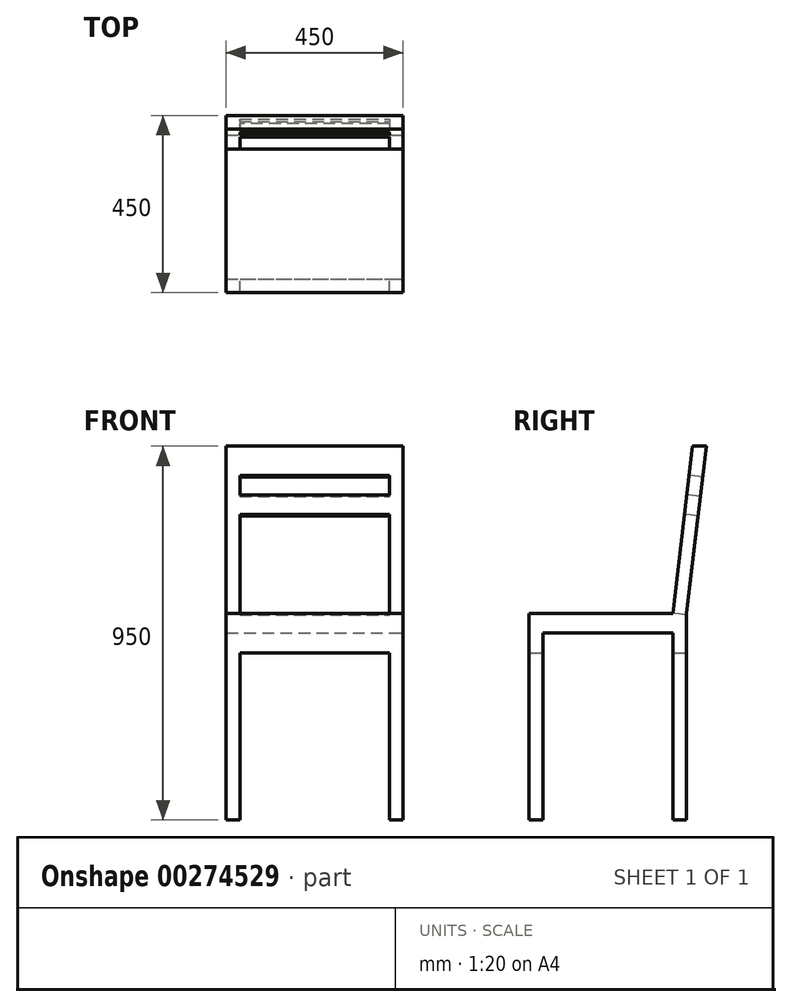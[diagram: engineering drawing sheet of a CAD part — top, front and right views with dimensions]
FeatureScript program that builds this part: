
annotation { "Feature Type Name" : "Feature", "Feature Type Description" : "" }
export const myFeature = defineFeature(function(context is Context, id is Id, definition is map)
    precondition{}
    {
        {
            var Q0;
            Q0=qCreatedBy(makeId("Top.planeOp"),FACE);
            var sketch = newSketch(context, id + "F0", { "sketchPlane" : qUnion([Q0])});
            skLineSegment(sketch, "E0.bottom", {"start": v(225, 225) * mm, "end": v(-225, 225) * mm});
            skLineSegment(sketch, "E0.top", {"start": v(225, -225) * mm, "end": v(-225, -225) * mm});
            skLineSegment(sketch, "E0.left", {"start": v(225, 225) * mm, "end": v(225, -225) * mm});
            skLineSegment(sketch, "E0.right", {"start": v(-225, 225) * mm, "end": v(-225, -225) * mm});
            skPoint(sketch, "E0.middle", {"position": v(0, 0) * mm});
            skSolve(sketch);
        }
        {
            var Q0;
            Q0=qSketchRegion(id+"F0",true);
            extrude(context, id + "F1", {"entities" : qUnion([Q0]), "depth" : 950 * mm});
        }
        {
            var Q0;
            Q0=makeQuery(id+"F1.opExtrude","SWEPT_FACE",FACE,{"disambiguationData":[OSD([sQuery(id+"F0.wireOp",EDGE,"E0.left")])]});
            var sketch = newSketch(context, id + "F2", { "sketchPlane" : qUnion([Q0])});
            skLineSegment(sketch, "E1.bottom", {"start": v(225, 475) * mm, "end": v(-225, 475) * mm});
            skLineSegment(sketch, "E1.top", {"start": v(225, 525) * mm, "end": v(-225, 525) * mm});
            skLineSegment(sketch, "E1.left", {"start": v(225, 475) * mm, "end": v(225, 525) * mm});
            skLineSegment(sketch, "E1.right", {"start": v(-225, 475) * mm, "end": v(-225, 525) * mm});
            skLineSegment(sketch, "E2", {"start": v(225, 950) * mm, "end": v(175, 525) * mm});
            skLineSegment(sketch, "E3", {"start": v(190, 950) * mm, "end": v(140, 525) * mm});
            skLineSegment(sketch, "E4", {"start": v(175, 525) * mm, "end": v(175, 0) * mm});
            skLineSegment(sketch, "E5", {"start": v(140, 525) * mm, "end": v(140, 0) * mm});
            skLineSegment(sketch, "E6.bottom", {"start": v(-225, 475) * mm, "end": v(-190, 475) * mm});
            skLineSegment(sketch, "E6.top", {"start": v(-225, 0) * mm, "end": v(-190, 0) * mm});
            skLineSegment(sketch, "E6.left", {"start": v(-225, 475) * mm, "end": v(-225, 0) * mm});
            skLineSegment(sketch, "E6.right", {"start": v(-190, 475) * mm, "end": v(-190, 0) * mm});
            skSolve(sketch);
        }
        {
            var Q0;
            {var subQ0=sQuery(id+"F2.wireOp",EDGE,"E1.left");Q0=makeQuery(id+"F2.imprint","IMPRINT",FACE,{"disambiguationData":[TD([[makeQuery(id+"F2.imprint","IMPRINT",EDGE,{"derivedFrom":subQ0}),-1.0]])]});}
            var Q1;
            {var subQ0=sQuery(id+"F2.wireOp",EDGE,"E6.right");Q1=makeQuery(id+"F2.imprint","IMPRINT",FACE,{"disambiguationData":[TD([[makeQuery(id+"F2.imprint","IMPRINT",EDGE,{"derivedFrom":subQ0}),1.0]])]});}
            var Q2;
            {var subQ1=sQuery(id+"F0.wireOp",EDGE,"E0.left");var subQ4=sQuery(id+"F2.wireOp",EDGE,"E4");var subQ6=makeQuery(id+"F1.opExtrude","CAP_EDGE",EDGE,{"disambiguationData":[OSD([subQ1])],"isStart":true});var subQ7=makeQuery(id+"F2.imprint","INTERSECT",VERTEX,{"derivedFrom":[subQ6,subQ4]});Q2=makeQuery(id+"F2.imprint","IMPRINT",FACE,{"disambiguationData":[TD([[makeQuery(id+"F2.imprint","IMPRINT",EDGE,{"disambiguationData":[TD([[subQ7,1.0]])],"derivedFrom":subQ4}),1.0]])]});}
            var Q3;
            {var subQ4=sQuery(id+"F2.wireOp",EDGE,"E2");Q3=makeQuery(id+"F2.imprint","IMPRINT",FACE,{"disambiguationData":[TD([[makeQuery(id+"F2.imprint","IMPRINT",EDGE,{"derivedFrom":subQ4}),1.0]])]});}
            var Q4;
            {var subQ4=sQuery(id+"F2.wireOp",EDGE,"E3");Q4=makeQuery(id+"F2.imprint","IMPRINT",FACE,{"disambiguationData":[TD([[makeQuery(id+"F2.imprint","IMPRINT",EDGE,{"derivedFrom":subQ4}),-1.0]])]});}
            extrude(context, id + "F3", {"entities" : qUnion([Q0, Q1, Q2, Q3, Q4]), "operationType" : NewBodyOperationType.REMOVE, "endBound" : BoundingType.THROUGH_ALL, "oppositeDirection" : true, "depth" : 25 * mm});
        }
        {
            var Q0;
            Q0=makeQuery(id+"F3.boolean.opBoolean","COPY",FACE,{"derivedFrom":makeQuery(id+"F3.opExtrude","SWEPT_FACE",FACE,{"disambiguationData":[OSD([sQuery(id+"F2.wireOp",EDGE,"E4")])]})});
            var sketch = newSketch(context, id + "F4", { "sketchPlane" : qUnion([Q0])});
            skLineSegment(sketch, "E7", {"start": v(-190, 0) * mm, "end": v(-190, 425) * mm});
            skLineSegment(sketch, "E8", {"start": v(-190, 425) * mm, "end": v(190, 425) * mm});
            skLineSegment(sketch, "E9", {"start": v(190, 425) * mm, "end": v(190, 0) * mm});
            skSolve(sketch);
        }
        {
            var Q0;
            Q0 = qSketchRegion(id + "F4", true);
            var Q1;
            {var subQ0=sQuery(id+"F4.wireOp",EDGE,"E7");Q1=makeQuery(id+"F4.imprint","IMPRINT",FACE,{"disambiguationData":[TD([[makeQuery(id+"F4.imprint","IMPRINT",EDGE,{"derivedFrom":subQ0}),-1.0]])]});}
            extrude(context, id + "F5", {"entities" : qUnion([Q0, Q1]), "operationType" : NewBodyOperationType.REMOVE, "endBound" : BoundingType.THROUGH_ALL, "oppositeDirection" : true, "depth" : 25 * mm});
        }
        {
            var Q0;
            Q0=makeQuery(id+"F3.boolean.opBoolean","COPY",FACE,{"derivedFrom":makeQuery(id+"F3.opExtrude","SWEPT_FACE",FACE,{"disambiguationData":[OSD([sQuery(id+"F2.wireOp",EDGE,"E3")])]})});
            var sketch = newSketch(context, id + "F6", { "sketchPlane" : qUnion([Q0])});
            skLineSegment(sketch, "E10", {"start": v(-190, 537.76) * mm, "end": v(-190, 890.7) * mm});
            skLineSegment(sketch, "E11", {"start": v(-190, 890.7) * mm, "end": v(190, 890.7) * mm});
            skLineSegment(sketch, "E12", {"start": v(190, 890.7) * mm, "end": v(190, 537.76) * mm});
            skLineSegment(sketch, "E13", {"start": v(-190, 840.7) * mm, "end": v(190, 840.7) * mm});
            skLineSegment(sketch, "E14", {"start": v(190, 790.7) * mm, "end": v(-190, 790.7) * mm});
            skSolve(sketch);
        }
        {
            var Q0;
            {var subQ0=sQuery(id+"F6.wireOp",EDGE,"E11");Q0=makeQuery(id+"F6.imprint","IMPRINT",FACE,{"disambiguationData":[TD([[makeQuery(id+"F6.imprint","IMPRINT",EDGE,{"derivedFrom":subQ0}),-1.0]])]});}
            var Q1;
            {var subQ3=sQuery(id+"F6.wireOp",EDGE,"E14");Q1=makeQuery(id+"F6.imprint","IMPRINT",FACE,{"disambiguationData":[TD([[makeQuery(id+"F6.imprint","IMPRINT",EDGE,{"derivedFrom":subQ3}),1.0]])]});}
            extrude(context, id + "F7", {"entities" : qUnion([Q0, Q1]), "operationType" : NewBodyOperationType.REMOVE, "endBound" : BoundingType.THROUGH_ALL, "oppositeDirection" : true, "depth" : 25 * mm});
        }
    });
